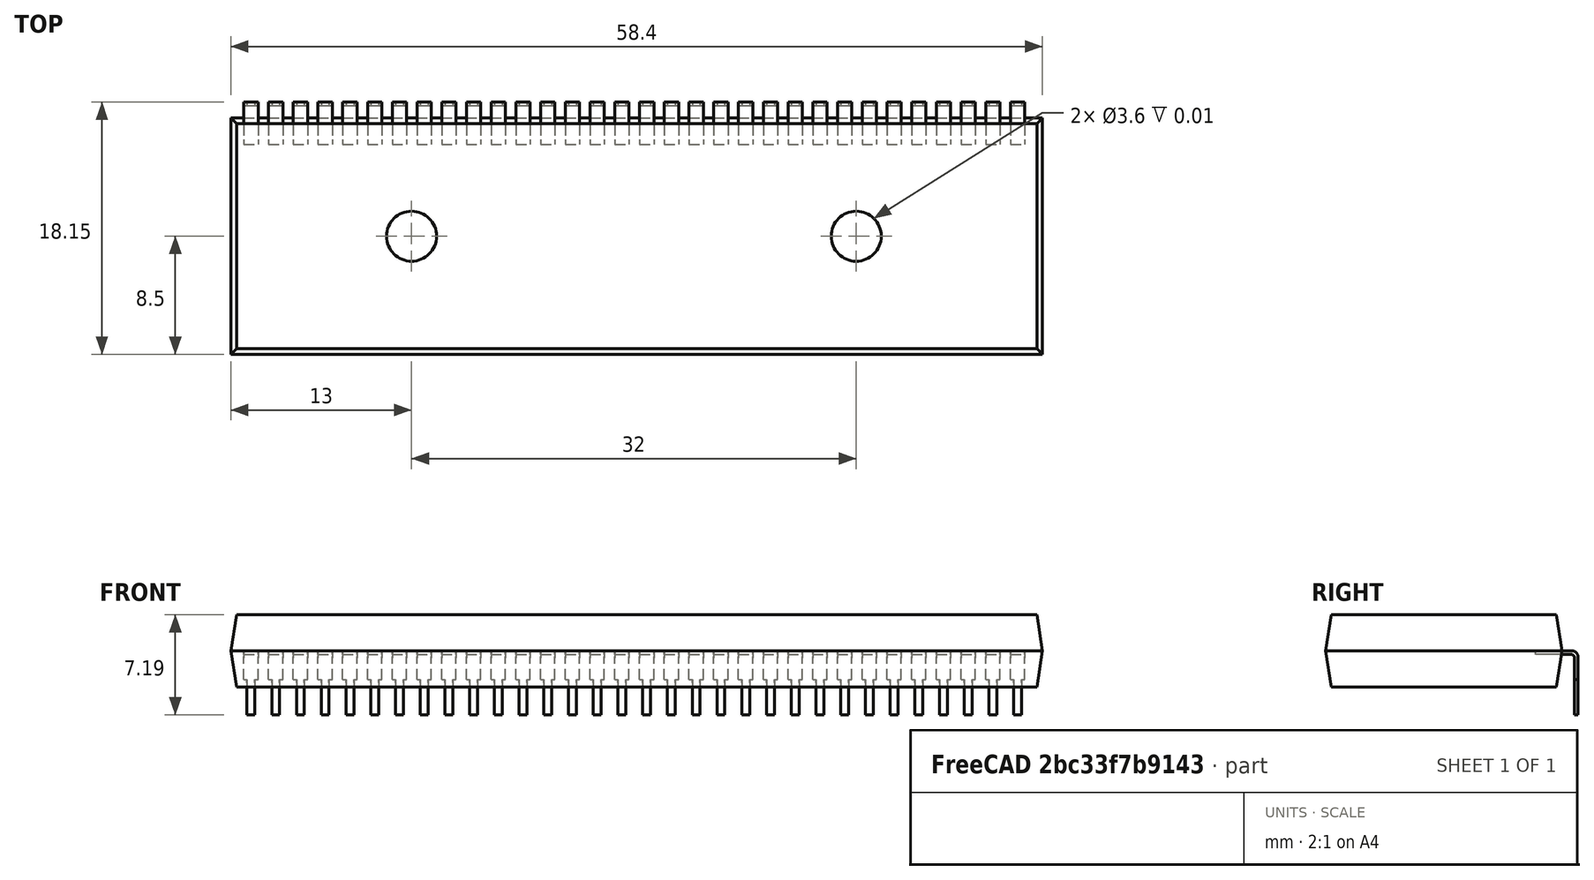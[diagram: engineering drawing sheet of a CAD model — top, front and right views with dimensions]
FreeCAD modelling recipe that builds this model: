
FCSTD DOCUMENT  (FreeCAD 0.19R24291 (Git))
Label: DIL-64
License: All rights reserved
LicenseURL: http://en.wikipedia.org/wiki/All_rights_reserved
objects: Part::Feature×32, PartDesign::Chamfer×8, PartDesign::SubtractiveCylinder×2, Sketcher::SketchObject×1, PartDesign::AdditiveBox×1, PartDesign::Body×1, Part::Compound×1, Part::Mirroring×1
note: 58 computed .brp shape members not serialized (recipe doc carries the construction recipe); baked Part::Feature solids carry a one-line shape summary decoded from their .brp

FEATURE [Sketcher::SketchObject] Sketch  label="Pads_Poly"
  FullyConstrained = false
  MapMode = 5
  Support = -> [XY_Plane]
  sketch-geometry (6):
    g0: LineSegment StartX=-29 StartY=8.55 StartZ=0 EndX=29 EndY=8.55 EndZ=0
    g1: LineSegment StartX=29.05 StartY=8.5 StartZ=0 EndX=29.05 EndY=-8.5 EndZ=0
    g2: LineSegment StartX=29 StartY=-8.55 StartZ=0 EndX=-29 EndY=-8.55 EndZ=0
    g3: LineSegment StartX=-29.05 StartY=-8.5 StartZ=0 EndX=-29.05 EndY=8.5 EndZ=0
    g4: ArcOfCircle CenterX=-29 CenterY=-9.373e-13 CenterZ=0 NormalX=0 NormalY=0 NormalZ=1 AngleXU=9.225e-13 Radius=0.966 StartAngle=0 EndAngle=1.51901
    g5: ArcOfCircle CenterX=-29 CenterY=3.3751e-12 CenterZ=0 NormalX=0 NormalY=0 NormalZ=1 AngleXU=-1.5708 Radius=0.966 StartAngle=0.051783 EndAngle=1.5708
FEATURE [PartDesign::AdditiveBox] Box
  AttacherType = Attacher::AttachEngine3D
  AttachmentOffset = pos=(-29,-8.5,2) rot=(0,0,1;0rad)
  Height = 5.19
  Length = 58.4
  MapMode = 5
  Placement = pos=(-29,-8.5,2) rot=(0,0,1;0rad)
  Support = -> [XY_Plane]
  Width = 17
FEATURE [PartDesign::Chamfer] Chamfer
  Angle = 45
  Base = -> Box [Edge2]
  BaseFeature = -> Box
  ChamferType = 1
  FlipDirection = false
  Placement = pos=(-29,-8.5,2) rot=(0,0,1;0rad)
  Size = 2.595
  Size2 = 0.4
  SupportTransform = false
FEATURE [PartDesign::Chamfer] Chamfer001
  Angle = 45
  Base = -> Chamfer [Edge3]
  BaseFeature = -> Chamfer
  ChamferType = 1
  FlipDirection = false
  Placement = pos=(-29,-8.5,2) rot=(0,0,1;0rad)
  Size = 2.594
  Size2 = 0.4
  SupportTransform = false
FEATURE [PartDesign::Chamfer] Chamfer002
  Angle = 45
  Base = -> Chamfer001 [Edge18]
  BaseFeature = -> Chamfer001
  ChamferType = 1
  FlipDirection = false
  Placement = pos=(-29,-8.5,2) rot=(0,0,1;0rad)
  Size = 0.4
  Size2 = 2.595
  SupportTransform = false
FEATURE [PartDesign::Chamfer] Chamfer003
  Angle = 45
  Base = -> Chamfer002 [Edge15]
  BaseFeature = -> Chamfer002
  ChamferType = 1
  FlipDirection = false
  Placement = pos=(-29,-8.5,2) rot=(0,0,1;0rad)
  Size = 2.594
  Size2 = 0.4
  SupportTransform = false
FEATURE [PartDesign::SubtractiveCylinder] Cylinder
  Angle = 360
  AttacherType = Attacher::AttachEngine3D
  AttachmentOffset = pos=(16,0,7.18) rot=(0,0,1;0rad)
  BaseFeature = -> Chamfer003
  Height = 0.01
  MapMode = 5
  Placement = pos=(16,0,7.18) rot=(0,0,1;0rad)
  Radius = 1.8
  Support = -> [XY_Plane]
FEATURE [PartDesign::SubtractiveCylinder] Cylinder001
  Angle = 360
  AttacherType = Attacher::AttachEngine3D
  AttachmentOffset = pos=(-16,0,7.18) rot=(0,0,1;0rad)
  BaseFeature = -> Cylinder
  Height = 0.01
  MapMode = 5
  Placement = pos=(-16,0,7.18) rot=(0,0,1;0rad)
  Radius = 1.8
  Support = -> [XY_Plane]
FEATURE [PartDesign::Chamfer] Chamfer004
  Angle = 45
  Base = -> Cylinder001 [Edge5]
  BaseFeature = -> Cylinder001
  ChamferType = 1
  FlipDirection = false
  Placement = pos=(-16,0,7.18) rot=(0,0,1;0rad)
  Size = 2.594
  Size2 = 0.4
  SupportTransform = false
FEATURE [PartDesign::Chamfer] Chamfer005
  Angle = 45
  Base = -> Chamfer004 [Edge7]
  BaseFeature = -> Chamfer004
  ChamferType = 1
  FlipDirection = false
  Placement = pos=(-16,0,7.18) rot=(0,0,1;0rad)
  Size = 2.594
  Size2 = 0.4
  SupportTransform = false
FEATURE [PartDesign::Chamfer] Chamfer006
  Angle = 45
  Base = -> Chamfer005 [Edge28]
  BaseFeature = -> Chamfer005
  ChamferType = 1
  FlipDirection = false
  Placement = pos=(-16,0,7.18) rot=(0,0,1;0rad)
  Size = 2.594
  Size2 = 0.4
  SupportTransform = false
FEATURE [PartDesign::Chamfer] Chamfer007
  Angle = 45
  Base = -> Chamfer006 [Edge20]
  BaseFeature = -> Chamfer006
  ChamferType = 1
  FlipDirection = false
  Placement = pos=(-16,0,7.18) rot=(0,0,1;0rad)
  Size = 2.594
  Size2 = 0.4
  SupportTransform = false
FEATURE [PartDesign::Body] Body
  Group = -> [Sketch,Box,Chamfer,Chamfer001,Chamfer002,Chamfer003,Cylinder,Cylinder001,Chamfer004,Chamfer005,Chamfer006,Chamfer007]
  Origin = -> Origin
  Tip = -> Chamfer007
FEATURE [Part::Feature] Solid
  shape: bbox 1.025 x 3.05 x 4.6 mm, 14 faces (baked)
FEATURE [Part::Feature] Solid001 .. Solid031  x31 (patterned run collapsed; names and placements below)
  shape: bbox 1.025 x 3.05 x 4.6 mm, 14 faces (baked)
  placements: 31 in arithmetic series — first pos=(1.78,0,0) rot=(0,0,1;0rad), step (1.78,0,0), last pos=(55.18,0,0) rot=(0,0,1;0rad)
FEATURE [Part::Compound] Compound
  Links = -> [Solid,Solid001,Solid002,Solid003,Solid004,Solid005,Solid006,Solid007,Solid008,Solid009,Solid010,Solid011,Solid012,Solid013,Solid014,Solid015,Solid016,Solid017,Solid018,Solid019,Solid020,Solid021,Solid022,Solid023,Solid024,Solid025,Solid026,Solid027,Solid028,Solid029,Solid030,Solid031]
FEATURE [Part::Mirroring] Part__Mirroring  label="Pins"
  Base = (0,0,0)
  Normal = (0,1,0)
  Source = -> Compound
